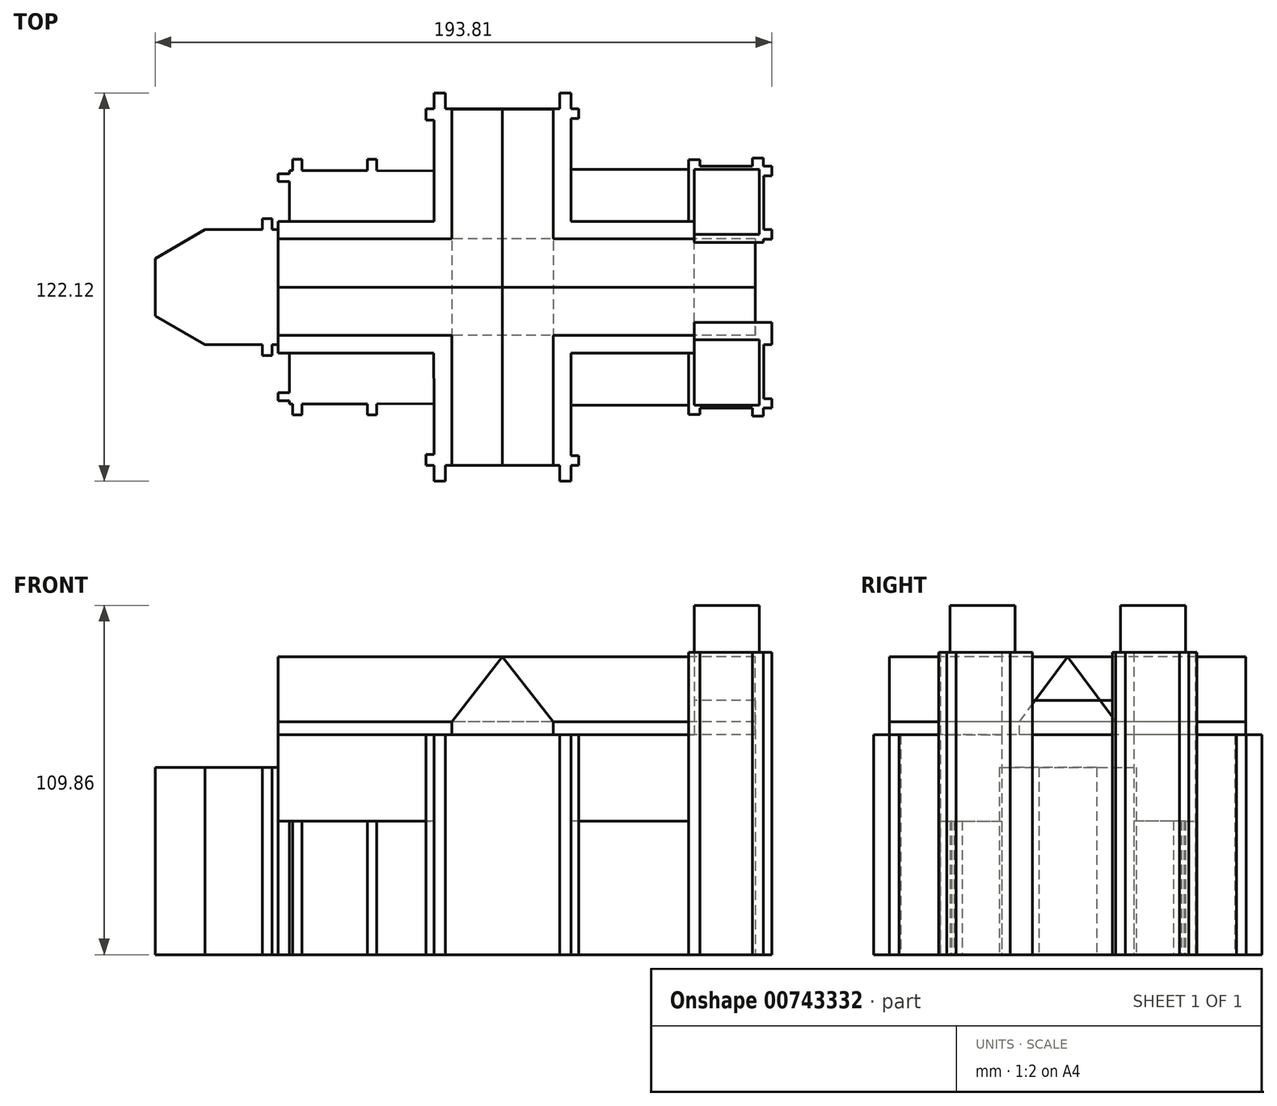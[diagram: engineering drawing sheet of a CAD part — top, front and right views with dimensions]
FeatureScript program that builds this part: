
annotation { "Feature Type Name" : "Feature", "Feature Type Description" : "" }
export const myFeature = defineFeature(function(context is Context, id is Id, definition is map)
    precondition{}
    {
        {
            var Q0;
            Q0=qCreatedBy(makeId("Top.planeOp"),FACE);
            var sketch = newSketch(context, id + "F0", { "sketchPlane" : qUnion([Q0])});
            skLineSegment(sketch, "E0", {"start": v(-2.62, 105.43) * mm, "end": v(-2.62, 102.93) * mm});
            skLineSegment(sketch, "E1", {"start": v(-2.62, 102.93) * mm, "end": v(0, 102.93) * mm});
            skLineSegment(sketch, "E2", {"start": v(0, 102.93) * mm, "end": v(0, 99.93) * mm});
            skLineSegment(sketch, "E3", {"start": v(-2.5, 99.93) * mm, "end": v(-2.5, 82.93) * mm});
            skLineSegment(sketch, "E4", {"start": v(-2.5, 82.93) * mm, "end": v(0, 82.93) * mm});
            skLineSegment(sketch, "E5", {"start": v(0, 82.93) * mm, "end": v(0, 79.93) * mm});
            skLineSegment(sketch, "E6", {"start": v(0, 79.93) * mm, "end": v(-2.62, 79.93) * mm});
            skLineSegment(sketch, "E7", {"start": v(-2.62, 105.43) * mm, "end": v(-6.12, 105.43) * mm});
            skLineSegment(sketch, "E8", {"start": v(-6.12, 105.43) * mm, "end": v(-6.12, 102.93) * mm});
            skLineSegment(sketch, "E9", {"start": v(-6.12, 102.93) * mm, "end": v(-22.62, 102.93) * mm});
            skLineSegment(sketch, "E10", {"start": v(-22.62, 102.93) * mm, "end": v(-22.62, 104.93) * mm});
            skLineSegment(sketch, "E11", {"start": v(-22.62, 104.93) * mm, "end": v(-26.12, 104.93) * mm});
            skLineSegment(sketch, "E12", {"start": v(-26.12, 104.93) * mm, "end": v(-26.12, 101.93) * mm});
            skLineSegment(sketch, "E13", {"start": v(-26.12, 101.93) * mm, "end": v(-63.12, 101.93) * mm});
            skLineSegment(sketch, "E14", {"start": v(-63.12, 101.93) * mm, "end": v(-63.12, 117.93) * mm});
            skLineSegment(sketch, "E15", {"start": v(-63.12, 117.93) * mm, "end": v(-60.62, 117.93) * mm});
            skLineSegment(sketch, "E16", {"start": v(-60.62, 117.93) * mm, "end": v(-60.62, 120.93) * mm});
            skLineSegment(sketch, "E17", {"start": v(-60.62, 120.93) * mm, "end": v(-63.12, 120.93) * mm});
            skLineSegment(sketch, "E18", {"start": v(-63.12, 120.93) * mm, "end": v(-63.12, 125.93) * mm});
            skLineSegment(sketch, "E19", {"start": v(-63.12, 125.93) * mm, "end": v(-66.62, 125.93) * mm});
            skLineSegment(sketch, "E20", {"start": v(-66.62, 125.93) * mm, "end": v(-66.62, 120.93) * mm});
            skLineSegment(sketch, "E21", {"start": v(-66.62, 120.93) * mm, "end": v(-102.62, 120.93) * mm});
            skLineSegment(sketch, "E22", {"start": v(-102.62, 120.93) * mm, "end": v(-102.62, 125.93) * mm});
            skLineSegment(sketch, "E23", {"start": v(-102.62, 125.93) * mm, "end": v(-106.12, 125.93) * mm});
            skLineSegment(sketch, "E24", {"start": v(-106.12, 125.93) * mm, "end": v(-106.12, 120.93) * mm});
            skLineSegment(sketch, "E25", {"start": v(-106.12, 120.93) * mm, "end": v(-108.62, 120.93) * mm});
            skLineSegment(sketch, "E26", {"start": v(-108.62, 120.93) * mm, "end": v(-108.62, 117.43) * mm});
            skLineSegment(sketch, "E27", {"start": v(-108.62, 117.43) * mm, "end": v(-106.12, 117.43) * mm});
            skLineSegment(sketch, "E28", {"start": v(-106.12, 117.43) * mm, "end": v(-106.12, 101.43) * mm});
            skLineSegment(sketch, "E29", {"start": v(-106.12, 101.43) * mm, "end": v(-124.12, 101.58) * mm});
            skLineSegment(sketch, "E30", {"start": v(-124.12, 101.58) * mm, "end": v(-124.12, 105.08) * mm});
            skLineSegment(sketch, "E31", {"start": v(-124.12, 105.08) * mm, "end": v(-127.12, 105.08) * mm});
            skLineSegment(sketch, "E32", {"start": v(-127.12, 105.08) * mm, "end": v(-127.12, 101.58) * mm});
            skLineSegment(sketch, "E33", {"start": v(-127.12, 101.58) * mm, "end": v(-147.62, 101.58) * mm});
            skLineSegment(sketch, "E34", {"start": v(-147.62, 101.58) * mm, "end": v(-147.62, 105.08) * mm});
            skLineSegment(sketch, "E35", {"start": v(-147.62, 105.08) * mm, "end": v(-150.62, 105.08) * mm});
            skLineSegment(sketch, "E36", {"start": v(-150.62, 105.08) * mm, "end": v(-150.62, 101.58) * mm});
            skLineSegment(sketch, "E37", {"start": v(-150.62, 101.58) * mm, "end": v(-151.62, 101.58) * mm});
            skLineSegment(sketch, "E38", {"start": v(-151.62, 101.58) * mm, "end": v(-151.62, 100.58) * mm});
            skLineSegment(sketch, "E39", {"start": v(-151.62, 100.58) * mm, "end": v(-155.12, 100.58) * mm});
            skLineSegment(sketch, "E40", {"start": v(-155.12, 100.58) * mm, "end": v(-155.12, 98.08) * mm});
            skLineSegment(sketch, "E41", {"start": v(-155.12, 98.08) * mm, "end": v(-151.62, 98.08) * mm});
            skLineSegment(sketch, "E42", {"start": v(-151.62, 98.08) * mm, "end": v(-151.62, 85.58) * mm});
            skLineSegment(sketch, "E43", {"start": v(-151.62, 85.58) * mm, "end": v(-155.12, 85.58) * mm});
            skLineSegment(sketch, "E44", {"start": v(-155.12, 85.58) * mm, "end": v(-155.12, 82.93) * mm});
            skLineSegment(sketch, "E45", {"start": v(-193.81, 73.9) * mm, "end": v(-178.18, 82.93) * mm});
            skLineSegment(sketch, "E46", {"start": v(-193.81, 73.9) * mm, "end": v(-193.81, 64.87) * mm});
            skLineSegment(sketch, "E47", {"start": v(-155.12, 82.93) * mm, "end": v(-157.12, 82.93) * mm});
            skLineSegment(sketch, "E48", {"start": v(-157.12, 82.93) * mm, "end": v(-157.12, 86.43) * mm});
            skLineSegment(sketch, "E49", {"start": v(-157.12, 86.43) * mm, "end": v(-160.12, 86.43) * mm});
            skLineSegment(sketch, "E50", {"start": v(-160.12, 86.43) * mm, "end": v(-160.12, 82.93) * mm});
            skLineSegment(sketch, "E51", {"start": v(-160.12, 82.93) * mm, "end": v(-178.18, 82.93) * mm});
            skLineSegment(sketch, "E52", {"start": v(-2.62, 79.93) * mm, "end": v(-2.62, 78.93) * mm});
            skLineSegment(sketch, "E53", {"start": v(-2.62, 78.93) * mm, "end": v(-5.12, 78.93) * mm});
            skLineSegment(sketch, "E54", {"start": v(-5.12, 78.93) * mm, "end": v(-5.12, 64.87) * mm});
            skLineSegment(sketch, "E55.MirrorCS", {"start": v(-193.81, 55.84) * mm, "end": v(-193.81, 64.87) * mm});
            skLineSegment(sketch, "E56.MirrorCS", {"start": v(-193.81, 55.84) * mm, "end": v(-178.18, 46.82) * mm});
            skLineSegment(sketch, "E57.MirrorCS", {"start": v(-160.12, 46.82) * mm, "end": v(-178.18, 46.82) * mm});
            skLineSegment(sketch, "E58.MirrorCS", {"start": v(-160.12, 43.32) * mm, "end": v(-160.12, 46.82) * mm});
            skLineSegment(sketch, "E59.MirrorCS", {"start": v(-157.12, 43.32) * mm, "end": v(-160.12, 43.32) * mm});
            skLineSegment(sketch, "E60.MirrorCS", {"start": v(-157.12, 46.82) * mm, "end": v(-157.12, 43.32) * mm});
            skLineSegment(sketch, "E61.MirrorCS", {"start": v(-155.12, 46.82) * mm, "end": v(-157.12, 46.82) * mm});
            skLineSegment(sketch, "E62.MirrorCS", {"start": v(-155.12, 44.17) * mm, "end": v(-155.12, 46.82) * mm});
            skLineSegment(sketch, "E63.MirrorCS", {"start": v(-151.62, 44.17) * mm, "end": v(-155.12, 44.17) * mm});
            skLineSegment(sketch, "E64.MirrorCS", {"start": v(-151.62, 31.67) * mm, "end": v(-151.62, 44.17) * mm});
            skLineSegment(sketch, "E65.MirrorCS", {"start": v(-155.12, 31.67) * mm, "end": v(-151.62, 31.67) * mm});
            skLineSegment(sketch, "E66.MirrorCS", {"start": v(-155.12, 29.17) * mm, "end": v(-155.12, 31.67) * mm});
            skLineSegment(sketch, "E67.MirrorCS", {"start": v(-151.62, 29.17) * mm, "end": v(-155.12, 29.17) * mm});
            skLineSegment(sketch, "E68.MirrorCS", {"start": v(-151.62, 28.17) * mm, "end": v(-151.62, 29.17) * mm});
            skLineSegment(sketch, "E69.MirrorCS", {"start": v(-150.62, 28.17) * mm, "end": v(-151.62, 28.17) * mm});
            skLineSegment(sketch, "E70.MirrorCS", {"start": v(-150.62, 24.67) * mm, "end": v(-150.62, 28.17) * mm});
            skLineSegment(sketch, "E71.MirrorCS", {"start": v(-147.62, 24.67) * mm, "end": v(-150.62, 24.67) * mm});
            skLineSegment(sketch, "E72.MirrorCS", {"start": v(-147.62, 28.17) * mm, "end": v(-147.62, 24.67) * mm});
            skLineSegment(sketch, "E73.MirrorCS", {"start": v(-127.12, 28.17) * mm, "end": v(-147.62, 28.17) * mm});
            skLineSegment(sketch, "E74.MirrorCS", {"start": v(-127.12, 24.67) * mm, "end": v(-127.12, 28.17) * mm});
            skLineSegment(sketch, "E75.MirrorCS", {"start": v(-124.12, 24.67) * mm, "end": v(-127.12, 24.67) * mm});
            skLineSegment(sketch, "E76.MirrorCS", {"start": v(-124.12, 28.17) * mm, "end": v(-124.12, 24.67) * mm});
            skLineSegment(sketch, "E77.MirrorCS", {"start": v(-106.12, 28.31) * mm, "end": v(-124.12, 28.17) * mm});
            skLineSegment(sketch, "E78.MirrorCS", {"start": v(-106.12, 12.31) * mm, "end": v(-106.12, 28.31) * mm});
            skLineSegment(sketch, "E79.MirrorCS", {"start": v(-108.62, 12.31) * mm, "end": v(-106.12, 12.31) * mm});
            skLineSegment(sketch, "E80.MirrorCS", {"start": v(-108.62, 8.81) * mm, "end": v(-108.62, 12.31) * mm});
            skLineSegment(sketch, "E81.MirrorCS", {"start": v(-106.12, 8.81) * mm, "end": v(-108.62, 8.81) * mm});
            skLineSegment(sketch, "E82.MirrorCS", {"start": v(-106.12, 3.81) * mm, "end": v(-106.12, 8.81) * mm});
            skLineSegment(sketch, "E83.MirrorCS", {"start": v(-102.62, 3.81) * mm, "end": v(-106.12, 3.81) * mm});
            skLineSegment(sketch, "E84.MirrorCS", {"start": v(-102.62, 8.81) * mm, "end": v(-102.62, 3.81) * mm});
            skLineSegment(sketch, "E85.MirrorCS", {"start": v(-66.62, 8.81) * mm, "end": v(-102.62, 8.81) * mm});
            skLineSegment(sketch, "E86.MirrorCS", {"start": v(-66.62, 3.81) * mm, "end": v(-66.62, 8.81) * mm});
            skLineSegment(sketch, "E87.MirrorCS", {"start": v(-63.12, 3.81) * mm, "end": v(-66.62, 3.81) * mm});
            skLineSegment(sketch, "E88.MirrorCS", {"start": v(-63.12, 8.81) * mm, "end": v(-63.12, 3.81) * mm});
            skLineSegment(sketch, "E89.MirrorCS", {"start": v(-60.62, 8.81) * mm, "end": v(-63.12, 8.81) * mm});
            skLineSegment(sketch, "E90.MirrorCS", {"start": v(-60.62, 11.81) * mm, "end": v(-60.62, 8.81) * mm});
            skLineSegment(sketch, "E91.MirrorCS", {"start": v(-63.12, 11.81) * mm, "end": v(-60.62, 11.81) * mm});
            skLineSegment(sketch, "E92.MirrorCS", {"start": v(-63.12, 27.81) * mm, "end": v(-63.12, 11.81) * mm});
            skLineSegment(sketch, "E93.MirrorCS", {"start": v(-26.12, 27.81) * mm, "end": v(-63.12, 27.81) * mm});
            skLineSegment(sketch, "E94.MirrorCS", {"start": v(-26.12, 24.81) * mm, "end": v(-26.12, 27.81) * mm});
            skLineSegment(sketch, "E95.MirrorCS", {"start": v(-22.62, 24.81) * mm, "end": v(-26.12, 24.81) * mm});
            skLineSegment(sketch, "E96.MirrorCS", {"start": v(-22.62, 26.81) * mm, "end": v(-22.62, 24.81) * mm});
            skLineSegment(sketch, "E97.MirrorCS", {"start": v(-6.12, 26.81) * mm, "end": v(-22.62, 26.81) * mm});
            skLineSegment(sketch, "E98.MirrorCS", {"start": v(-6.12, 24.31) * mm, "end": v(-6.12, 26.81) * mm});
            skLineSegment(sketch, "E99.MirrorCS", {"start": v(-2.62, 24.31) * mm, "end": v(-6.12, 24.31) * mm});
            skLineSegment(sketch, "E100.MirrorCS", {"start": v(-2.62, 24.31) * mm, "end": v(-2.62, 26.81) * mm});
            skLineSegment(sketch, "E101.MirrorCS", {"start": v(-2.62, 26.81) * mm, "end": v(0, 26.82) * mm});
            skLineSegment(sketch, "E102.MirrorCS", {"start": v(-2.5, 29.82) * mm, "end": v(-2.5, 46.82) * mm});
            skLineSegment(sketch, "E103.MirrorCS", {"start": v(-2.5, 29.82) * mm, "end": v(0, 29.82) * mm, "construction": true});
            skLineSegment(sketch, "E104.MirrorCS", {"start": v(-2.5, 46.82) * mm, "end": v(0, 46.82) * mm});
            skLineSegment(sketch, "E105", {"start": v(0, 99.93) * mm, "end": v(-2.5, 99.93) * mm});
            skLineSegment(sketch, "E106.MirrorCS", {"start": v(0, 29.82) * mm, "end": v(-2.5, 29.82) * mm});
            skLineSegment(sketch, "E107", {"start": v(0, 29.82) * mm, "end": v(0, 26.82) * mm});
            skLineSegment(sketch, "E108", {"start": v(0, 46.82) * mm, "end": v(0, 53.82) * mm});
            skLineSegment(sketch, "E109", {"start": v(0, 53.82) * mm, "end": v(-5.12, 53.82) * mm});
            skLineSegment(sketch, "E110", {"start": v(-5.12, 64.87) * mm, "end": v(-5.12, 53.82) * mm});
            skLineSegment(sketch, "E111", {"start": v(-193.81, 64.87) * mm, "end": v(-5.12, 64.87) * mm, "construction": true});
            skLineSegment(sketch, "E112", {"start": v(-106.12, 101.43) * mm, "end": v(-106.12, 85.58) * mm});
            skLineSegment(sketch, "E113", {"start": v(-63.12, 101.93) * mm, "end": v(-63.12, 85.58) * mm});
            skLineSegment(sketch, "E114", {"start": v(-106.12, 28.31) * mm, "end": v(-106.25, 44.17) * mm});
            skLineSegment(sketch, "E115", {"start": v(-63.12, 27.81) * mm, "end": v(-63.12, 44.17) * mm});
            skLineSegment(sketch, "E116.bottom", {"start": v(-24.37, 27.81) * mm, "end": v(-3.87, 27.81) * mm});
            skLineSegment(sketch, "E116.top", {"start": v(-24.37, 48.31) * mm, "end": v(-3.87, 48.31) * mm});
            skLineSegment(sketch, "E116.left", {"start": v(-24.37, 27.81) * mm, "end": v(-24.37, 48.31) * mm});
            skLineSegment(sketch, "E116.right", {"start": v(-3.87, 27.81) * mm, "end": v(-3.87, 48.31) * mm});
            skLineSegment(sketch, "E117.MirrorCS", {"start": v(-24.37, 81.43) * mm, "end": v(-3.87, 81.43) * mm});
            skLineSegment(sketch, "E118.MirrorCS", {"start": v(-3.87, 101.93) * mm, "end": v(-3.87, 81.43) * mm});
            skLineSegment(sketch, "E119.MirrorCS", {"start": v(-24.37, 101.93) * mm, "end": v(-3.87, 101.93) * mm});
            skLineSegment(sketch, "E120.MirrorCS", {"start": v(-24.37, 101.93) * mm, "end": v(-24.37, 81.43) * mm});
            skLineSegment(sketch, "E121.bottom", {"start": v(-155.12, 44.17) * mm, "end": v(-24.37, 44.17) * mm});
            skLineSegment(sketch, "E121.top", {"start": v(-155.12, 85.58) * mm, "end": v(-24.37, 85.58) * mm});
            skLineSegment(sketch, "E121.left", {"start": v(-155.12, 44.17) * mm, "end": v(-155.12, 85.58) * mm});
            skLineSegment(sketch, "E121.right", {"start": v(-24.37, 44.17) * mm, "end": v(-24.37, 85.58) * mm});
            skLineSegment(sketch, "E122", {"start": v(-5.12, 53.82) * mm, "end": v(-24.37, 53.82) * mm});
            skLineSegment(sketch, "E123", {"start": v(-5.12, 78.93) * mm, "end": v(-24.37, 78.93) * mm});
            skLineSegment(sketch, "E124", {"start": v(-26.12, 101.93) * mm, "end": v(-26.12, 85.58) * mm});
            skLineSegment(sketch, "E125", {"start": v(-26.12, 27.81) * mm, "end": v(-26.12, 44.17) * mm});
            skSolve(sketch);
        }
        {
            var Q0;
            Q0=makeQuery(id+"F0.imprint","IMPRINT",FACE,{"disambiguationData":[TD([[makeQuery(id+"F0.imprint","IMPRINT",EDGE,{"derivedFrom":sQuery(id+"F0.wireOp",EDGE,"E45")}),-1.0]])]});
            extrude(context, id + "F1", {"entities" : qUnion([Q0]), "depth" : 58.87 * mm, "offsetDistance" : 25 * mm});
        }
        {
            var Q0;
            {var subQ12=sQuery(id+"F0.wireOp",EDGE,"E43");Q0=makeQuery(id+"F0.imprint","IMPRINT",FACE,{"disambiguationData":[TD([[makeQuery(id+"F0.imprint","IMPRINT",EDGE,{"derivedFrom":subQ12}),1.0]])]});}
            var Q1;
            Q1=makeQuery(id+"F0.imprint","IMPRINT",FACE,{"disambiguationData":[TD([[makeQuery(id+"F0.imprint","IMPRINT",EDGE,{"derivedFrom":sQuery(id+"F0.wireOp",EDGE,"E14")}),1.0]])]});
            var Q2;
            Q2=makeQuery(id+"F0.imprint","IMPRINT",FACE,{"disambiguationData":[TD([[makeQuery(id+"F0.imprint","IMPRINT",EDGE,{"derivedFrom":sQuery(id+"F0.wireOp",EDGE,"E78.MirrorCS")}),-1.0]])]});
            extrude(context, id + "F2", {"entities" : qUnion([Q0, Q1, Q2]), "operationType" : NewBodyOperationType.ADD, "depth" : 69.14 * mm, "offsetDistance" : 25 * mm});
        }
        {
            var Q0;
            {var subQ3=sQuery(id+"F0.wireOp",EDGE,"E117.MirrorCS");Q0=makeQuery(id+"F0.imprint","IMPRINT",FACE,{"disambiguationData":[TD([[makeQuery(id+"F0.imprint","IMPRINT",EDGE,{"derivedFrom":subQ3}),1.0]])]});}
            var Q1;
            {var subQ3=sQuery(id+"F0.wireOp",EDGE,"E116.bottom");Q1=makeQuery(id+"F0.imprint","IMPRINT",FACE,{"disambiguationData":[TD([[makeQuery(id+"F0.imprint","IMPRINT",EDGE,{"derivedFrom":subQ3}),1.0]])]});}
            extrude(context, id + "F3", {"entities" : qUnion([Q0, Q1]), "operationType" : NewBodyOperationType.ADD, "depth" : 109.86 * mm, "offsetDistance" : 25 * mm});
        }
        {
            var Q0;
            Q0=makeQuery(id+"F0.imprint","IMPRINT",FACE,{"disambiguationData":[TD([[makeQuery(id+"F0.imprint","IMPRINT",EDGE,{"derivedFrom":sQuery(id+"F0.wireOp",EDGE,"E94.MirrorCS")}),-1.0]])]});
            var Q1;
            Q1=makeQuery(id+"F0.imprint","IMPRINT",FACE,{"disambiguationData":[TD([[makeQuery(id+"F0.imprint","IMPRINT",EDGE,{"derivedFrom":sQuery(id+"F0.wireOp",EDGE,"E0")}),-1.0]])]});
            extrude(context, id + "F4", {"entities" : qUnion([Q0, Q1]), "operationType" : NewBodyOperationType.ADD, "depth" : 95.04 * mm, "offsetDistance" : 25 * mm});
        }
        {
            var Q0;
            Q0=makeQuery(id+"F0.imprint","IMPRINT",FACE,{"disambiguationData":[TD([[makeQuery(id+"F0.imprint","IMPRINT",EDGE,{"derivedFrom":sQuery(id+"F0.wireOp",EDGE,"E13")}),1.0]])]});
            var Q1;
            Q1=makeQuery(id+"F0.imprint","IMPRINT",FACE,{"disambiguationData":[TD([[makeQuery(id+"F0.imprint","IMPRINT",EDGE,{"derivedFrom":sQuery(id+"F0.wireOp",EDGE,"E29")}),1.0]])]});
            var Q2;
            Q2=makeQuery(id+"F0.imprint","IMPRINT",FACE,{"disambiguationData":[TD([[makeQuery(id+"F0.imprint","IMPRINT",EDGE,{"derivedFrom":sQuery(id+"F0.wireOp",EDGE,"E93.MirrorCS")}),-1.0]])]});
            var Q3;
            {var subQ0=sQuery(id+"F0.wireOp",EDGE,"E64.MirrorCS");Q3=makeQuery(id+"F0.imprint","IMPRINT",FACE,{"disambiguationData":[TD([[makeQuery(id+"F0.imprint","IMPRINT",EDGE,{"derivedFrom":subQ0}),-1.0]])]});}
            extrude(context, id + "F5", {"entities" : qUnion([Q0, Q1, Q2, Q3]), "operationType" : NewBodyOperationType.ADD, "depth" : 42.05 * mm, "offsetDistance" : 25 * mm});
        }
        {
            var Q0;
            Q0=makeQuery(id+"F0.imprint","IMPRINT",FACE,{"disambiguationData":[TD([[makeQuery(id+"F0.imprint","IMPRINT",EDGE,{"derivedFrom":sQuery(id+"F0.wireOp",EDGE,"E54")}),-1.0]])]});
            extrude(context, id + "F6", {"entities" : qUnion([Q0]), "operationType" : NewBodyOperationType.ADD, "depth" : 79.96 * mm, "offsetDistance" : 25 * mm});
        }
        {
            var Q0;
            Q0=makeQuery(id+"F2.opExtrude","SWEPT_FACE",FACE,{"disambiguationData":[OSD([sQuery(id+"F0.wireOp",EDGE,"E44"),sQuery(id+"F0.wireOp",EDGE,"E62.MirrorCS"),sQuery(id+"F0.wireOp",EDGE,"E121.left")])]});
            var sketch = newSketch(context, id + "F7", { "sketchPlane" : qUnion([Q0])});
            skLineSegment(sketch, "E126", {"start": v(-64.87, 69.14) * mm, "end": v(-64.87, 93.7) * mm, "construction": true});
            skLineSegment(sketch, "E127", {"start": v(-85.58, 69.14) * mm, "end": v(-80.07, 69.14) * mm});
            skLineSegment(sketch, "E128", {"start": v(-80.07, 69.14) * mm, "end": v(-80.07, 73.27) * mm});
            skLineSegment(sketch, "E129", {"start": v(-80.07, 73.27) * mm, "end": v(-64.87, 93.7) * mm});
            skLineSegment(sketch, "E130.MirrorCS", {"start": v(-49.68, 73.27) * mm, "end": v(-64.87, 93.7) * mm});
            skLineSegment(sketch, "E131.MirrorCS", {"start": v(-49.68, 69.14) * mm, "end": v(-49.68, 73.27) * mm});
            skLineSegment(sketch, "E132.MirrorCS", {"start": v(-44.17, 69.14) * mm, "end": v(-49.68, 69.14) * mm});
            skLineSegment(sketch, "E133", {"start": v(-80.07, 69.14) * mm, "end": v(-49.68, 69.14) * mm});
            skSolve(sketch);
        }
        {
            var Q0;
            Q0 = qSketchRegion(id + "F7", true);
            extrude(context, id + "F8", {"entities" : qUnion([Q0]), "oppositeDirection" : true, "depth" : 150 * mm, "offsetDistance" : 25 * mm});
        }
        {
            var Q0;
            Q0=makeQuery(id+"F2.opExtrude","SWEPT_FACE",FACE,{"disambiguationData":[OSD([sQuery(id+"F0.wireOp",EDGE,"E85.MirrorCS")])]});
            var sketch = newSketch(context, id + "F9", { "sketchPlane" : qUnion([Q0])});
            skLineSegment(sketch, "E134", {"start": v(-106.12, 69.14) * mm, "end": v(-100.6, 69.14) * mm});
            skLineSegment(sketch, "E135", {"start": v(-100.6, 69.14) * mm, "end": v(-100.6, 73.27) * mm});
            skLineSegment(sketch, "E136", {"start": v(-100.6, 73.27) * mm, "end": v(-84.62, 93.7) * mm});
            skLineSegment(sketch, "E137.MirrorCS", {"start": v(-68.63, 73.27) * mm, "end": v(-84.62, 93.7) * mm});
            skLineSegment(sketch, "E138.MirrorCS", {"start": v(-68.63, 69.14) * mm, "end": v(-68.63, 73.27) * mm});
            skLineSegment(sketch, "E139.MirrorCS", {"start": v(-63.12, 69.14) * mm, "end": v(-68.63, 69.14) * mm});
            skLineSegment(sketch, "E140", {"start": v(-100.6, 69.14) * mm, "end": v(-68.63, 69.14) * mm});
            skSolve(sketch);
        }
        {
            var Q0;
            Q0 = qSketchRegion(id + "F9", true);
            extrude(context, id + "F10", {"entities" : qUnion([Q0]), "oppositeDirection" : true, "depth" : 112 * mm, "offsetDistance" : 25 * mm});
        }
    });
